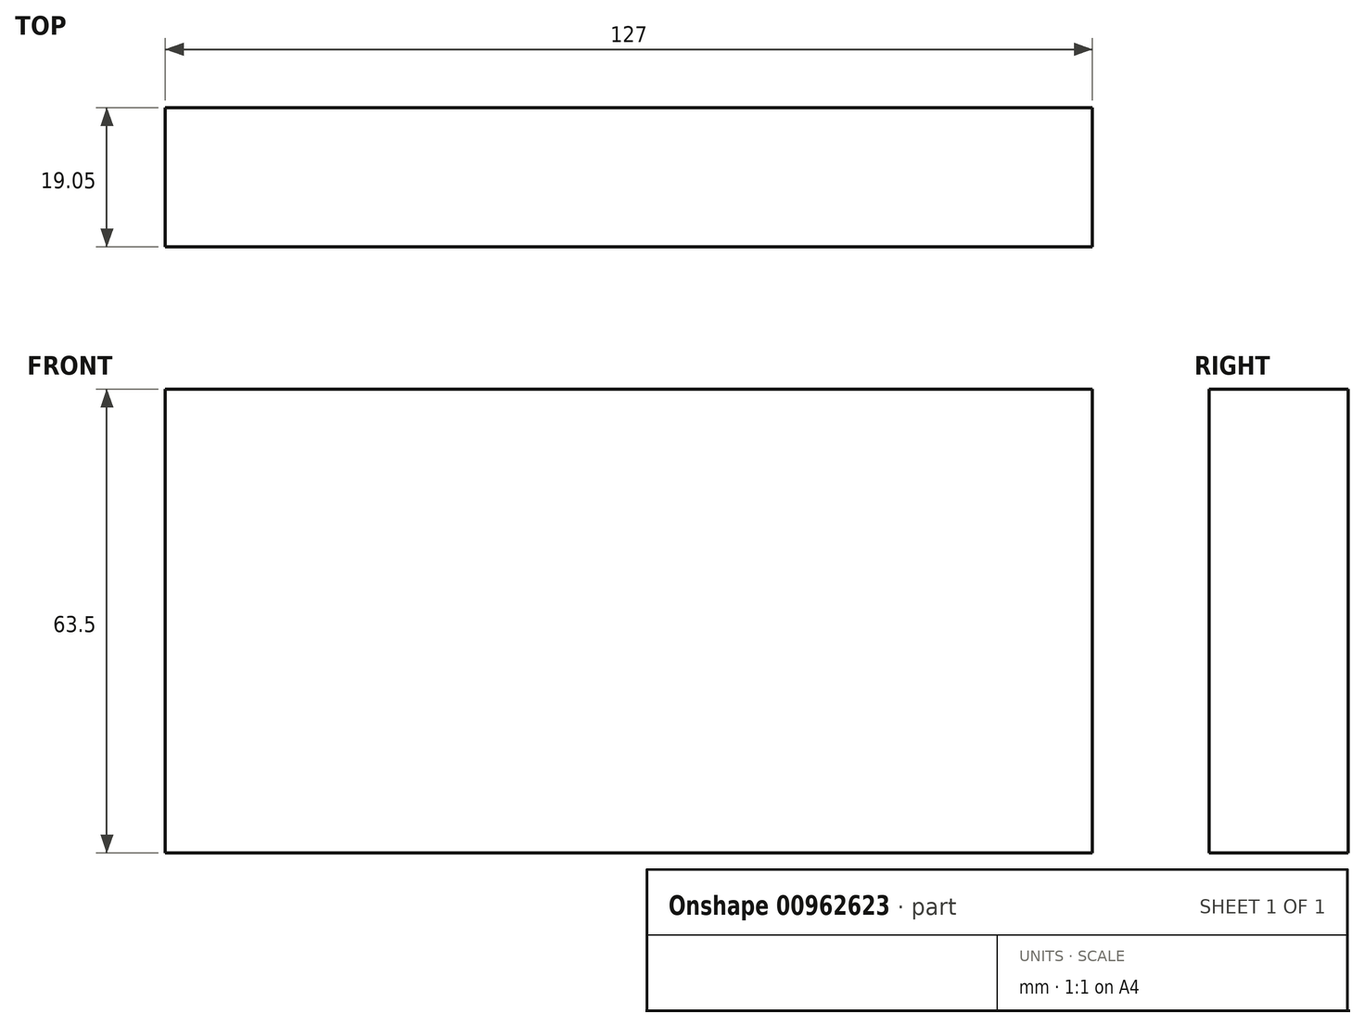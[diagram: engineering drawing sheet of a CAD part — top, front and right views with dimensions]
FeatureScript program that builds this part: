
annotation { "Feature Type Name" : "Feature", "Feature Type Description" : "" }
export const myFeature = defineFeature(function(context is Context, id is Id, definition is map)
    precondition{}
    {
        {
            var Q0;
            Q0=qCreatedBy(makeId("Front.planeOp"),FACE);
            var sketch = newSketch(context, id + "F0", { "sketchPlane" : qUnion([Q0])});
            skLineSegment(sketch, "E0.bottom", {"start": v(63.5, -29.3) * mm, "end": v(-63.5, -29.3) * mm});
            skLineSegment(sketch, "E0.top", {"start": v(63.5, 34.2) * mm, "end": v(-63.5, 34.2) * mm});
            skLineSegment(sketch, "E0.left", {"start": v(63.5, -29.3) * mm, "end": v(63.5, 34.2) * mm});
            skLineSegment(sketch, "E0.right", {"start": v(-63.5, -29.3) * mm, "end": v(-63.5, 34.2) * mm});
            skPoint(sketch, "E0.middle", {"position": v(0, 2.45) * mm});
            skSolve(sketch);
        }
        {
            var Q0;
            Q0=makeQuery(id+"F0.imprint","IMPRINT",FACE,{"disambiguationData":[TD([[makeQuery(id+"F0.imprint","IMPRINT",EDGE,{"derivedFrom":sQuery(id+"F0.wireOp",EDGE,"E0.bottom")}),-1.0]])]});
            extrude(context, id + "F1", {"entities" : qUnion([Q0]), "depth" : 19.05 * mm, "offsetDistance" : 25.4 * mm});
        }
    });
